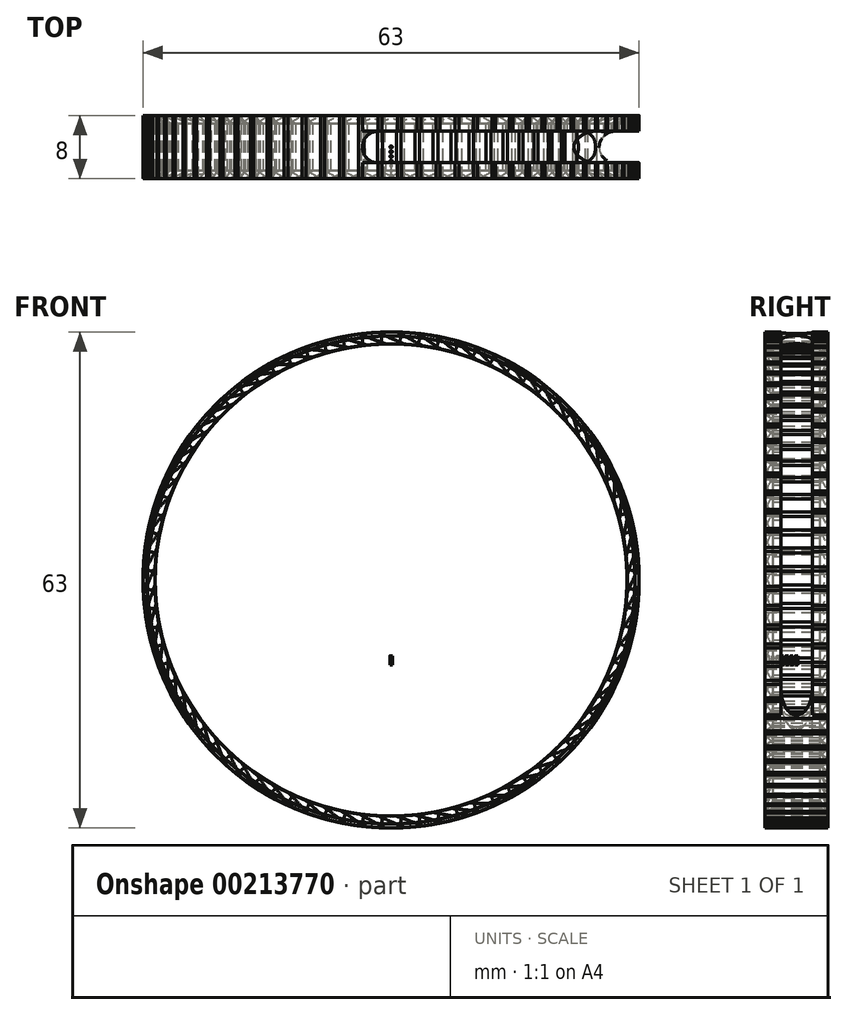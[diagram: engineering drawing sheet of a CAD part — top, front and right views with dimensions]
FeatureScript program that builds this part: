
annotation { "Feature Type Name" : "Feature", "Feature Type Description" : "" }
export const myFeature = defineFeature(function(context is Context, id is Id, definition is map)
    precondition{}
    {
        {
            var Q0;
            Q0=qCreatedBy(makeId("Front.planeOp"),FACE);
            var sketch = newSketch(context, id + "F0", { "sketchPlane" : qUnion([Q0])});
            skCircle(sketch, "E0", {"center": v(0, 0) * mm, "radius": 30 * mm});
            skCircle(sketch, "E1.0", {"center": v(0, 0) * mm, "radius": 31.5 * mm});
            skLineSegment(sketch, "E2.bottom", {"start": v(3.63, 31.29) * mm, "end": v(-3.63, 31.29) * mm, "construction": true});
            skLineSegment(sketch, "E2.top", {"start": v(3.63, 33.45) * mm, "end": v(-3.63, 33.45) * mm});
            skLineSegment(sketch, "E2.left", {"start": v(3.63, 31.29) * mm, "end": v(3.63, 33.45) * mm});
            skLineSegment(sketch, "E2.right", {"start": v(-3.63, 31.29) * mm, "end": v(-3.63, 33.45) * mm});
            skPoint(sketch, "E2.middle", {"position": v(0, 32.37) * mm});
            skLineSegment(sketch, "E3.1.0", {"start": v(6.4, -37.09) * mm, "end": v(4.54, -38.16) * mm});
            skLineSegment(sketch, "E3.1.1", {"start": v(2.77, -30.8) * mm, "end": v(0.9, -31.87) * mm});
            skLineSegment(sketch, "E3.1.2", {"start": v(0.9, -31.87) * mm, "end": v(4.54, -38.16) * mm});
            skLineSegment(sketch, "E3.1.3", {"start": v(2.77, -30.8) * mm, "end": v(6.4, -37.09) * mm, "construction": true});
            skLineSegment(sketch, "E3.2.0", {"start": v(60.6, 5.8) * mm, "end": v(62.47, 4.72) * mm});
            skLineSegment(sketch, "E3.2.1", {"start": v(56.97, -0.5) * mm, "end": v(58.84, -1.58) * mm});
            skLineSegment(sketch, "E3.2.2", {"start": v(58.84, -1.58) * mm, "end": v(62.47, 4.72) * mm});
            skLineSegment(sketch, "E3.2.3", {"start": v(56.97, -0.5) * mm, "end": v(60.6, 5.8) * mm, "construction": true});
            skPoint(sketch, "E3.center", {"position": v(21.12, 0) * mm});
            skLineSegment(sketch, "E4", {"start": v(0, 0) * mm, "end": v(22.27, 22.27) * mm, "construction": true});
            skLineSegment(sketch, "E5", {"start": v(0, 0) * mm, "end": v(-22.27, 22.27) * mm, "construction": true});
            skLineSegment(sketch, "E6.MirrorCS", {"start": v(0, 0) * mm, "end": v(22.27, -22.27) * mm, "construction": true});
            skLineSegment(sketch, "E7.MirrorCS", {"start": v(0, 0) * mm, "end": v(-22.27, -22.27) * mm, "construction": true});
            skLineSegment(sketch, "E8.0", {"start": v(-0.14, 0.14) * mm, "end": v(0, 0.28) * mm});
            skLineSegment(sketch, "E9.MirrorCS", {"start": v(0.14, -0.14) * mm, "end": v(0.28, 0) * mm});
            skLineSegment(sketch, "E10.MirrorCS", {"start": v(0.14, 0.14) * mm, "end": v(0, 0.28) * mm});
            skLineSegment(sketch, "E11.MirrorCS", {"start": v(-0.14, -0.14) * mm, "end": v(-0.28, 0) * mm});
            skLineSegment(sketch, "E12.MirrorCS", {"start": v(0.14, 0.14) * mm, "end": v(0.28, 0) * mm});
            skLineSegment(sketch, "E13.MirrorCS", {"start": v(-0.14, -0.14) * mm, "end": v(0, -0.28) * mm});
            skLineSegment(sketch, "E14.MirrorCS", {"start": v(0.14, -0.14) * mm, "end": v(0, -0.28) * mm});
            skLineSegment(sketch, "E15.MirrorCS", {"start": v(-0.14, 0.14) * mm, "end": v(-0.28, 0) * mm});
            skLineSegment(sketch, "E16.trimOffspring", {"start": v(-7.2, -7.48) * mm, "end": v(-21.07, -21.35) * mm, "construction": true});
            skLineSegment(sketch, "E17.trimOffspring", {"start": v(-7.48, -7.2) * mm, "end": v(-21.35, -21.07) * mm, "construction": true});
            skLineSegment(sketch, "E18.trimOffspring", {"start": v(-7.48, 7.2) * mm, "end": v(-21.35, 21.07) * mm, "construction": true});
            skLineSegment(sketch, "E19.trimOffspring", {"start": v(-7.2, 7.48) * mm, "end": v(-21.07, 21.35) * mm, "construction": true});
            skLineSegment(sketch, "E20.trimOffspring", {"start": v(7.2, 7.48) * mm, "end": v(21.07, 21.35) * mm, "construction": true});
            skLineSegment(sketch, "E21.trimOffspring", {"start": v(7.48, 7.2) * mm, "end": v(21.35, 21.07) * mm, "construction": true});
            skLineSegment(sketch, "E22.trimOffspring", {"start": v(7.2, -7.48) * mm, "end": v(21.07, -21.35) * mm, "construction": true});
            skLineSegment(sketch, "E23.trimOffspring", {"start": v(7.48, -7.2) * mm, "end": v(21.35, -21.07) * mm, "construction": true});
            skLineSegment(sketch, "E24", {"start": v(-3.63, 31.29) * mm, "end": v(-3.63, 28.18) * mm});
            skLineSegment(sketch, "E25", {"start": v(-3.63, 28.18) * mm, "end": v(3.63, 28.18) * mm});
            skLineSegment(sketch, "E26", {"start": v(3.63, 28.18) * mm, "end": v(3.63, 31.29) * mm});
            skLineSegment(sketch, "E27", {"start": v(70.64, 0) * mm, "end": v(60.6, 5.8) * mm});
            skLineSegment(sketch, "E28", {"start": v(56.97, -0.5) * mm, "end": v(28.25, 16.09) * mm});
            skLineSegment(sketch, "E29", {"start": v(28.25, 16.09) * mm, "end": v(70.64, 0) * mm});
            skLineSegment(sketch, "E30", {"start": v(6.4, -37.09) * mm, "end": v(35.16, -20.48) * mm});
            skLineSegment(sketch, "E31", {"start": v(2.77, -30.8) * mm, "end": v(31.56, -14.17) * mm});
            skLineSegment(sketch, "E32", {"start": v(31.56, -14.17) * mm, "end": v(35.16, -20.48) * mm});
            skSolve(sketch);
        }
        {
            var Q0;
            Q0=makeQuery(id+"F0.imprint","IMPRINT",FACE,{"disambiguationData":[TD([[makeQuery(id+"F0.imprint","IMPRINT",EDGE,{"derivedFrom":sQuery(id+"F0.wireOp",EDGE,"E0")}),-1.0]])]});
            var Q1;
            {var subQ2=sQuery(id+"F0.wireOp",EDGE,"E16.trimOffspring");var subQ7=sQuery(id+"F0.wireOp",EDGE,"E0");var subQ9=makeQuery(id+"F0.imprint","INTERSECT",VERTEX,{"derivedFrom":[subQ7,subQ2]});Q1=makeQuery(id+"F0.imprint","IMPRINT",FACE,{"disambiguationData":[TD([[makeQuery(id+"F0.imprint","IMPRINT",EDGE,{"disambiguationData":[TD([[subQ9,-1.0]])],"derivedFrom":subQ7}),-1.0]])]});}
            var Q2;
            {var subQ5=sQuery(id+"F0.wireOp",EDGE,"E21.trimOffspring");var subQ7=sQuery(id+"F0.wireOp",EDGE,"E0");var subQ8=makeQuery(id+"F0.imprint","INTERSECT",VERTEX,{"derivedFrom":[subQ7,subQ5]});Q2=makeQuery(id+"F0.imprint","IMPRINT",FACE,{"disambiguationData":[TD([[makeQuery(id+"F0.imprint","IMPRINT",EDGE,{"disambiguationData":[TD([[subQ8,1.0]])],"derivedFrom":subQ7}),-1.0]])]});}
            var Q3;
            {var subQ2=sQuery(id+"F0.wireOp",EDGE,"E19.trimOffspring");var subQ7=sQuery(id+"F0.wireOp",EDGE,"E0");var subQ8=makeQuery(id+"F0.imprint","INTERSECT",VERTEX,{"derivedFrom":[subQ7,subQ2]});Q3=makeQuery(id+"F0.imprint","IMPRINT",FACE,{"disambiguationData":[TD([[makeQuery(id+"F0.imprint","IMPRINT",EDGE,{"disambiguationData":[TD([[subQ8,1.0]])],"derivedFrom":subQ7}),-1.0]])]});}
            var Q4;
            {var subQ5=sQuery(id+"F0.wireOp",EDGE,"E17.trimOffspring");var subQ6=sQuery(id+"F0.wireOp",EDGE,"E0");var subQ7=makeQuery(id+"F0.imprint","INTERSECT",VERTEX,{"derivedFrom":[subQ6,subQ5]});Q4=makeQuery(id+"F0.imprint","IMPRINT",FACE,{"disambiguationData":[TD([[makeQuery(id+"F0.imprint","IMPRINT",EDGE,{"disambiguationData":[TD([[subQ7,1.0]])],"derivedFrom":subQ6}),-1.0]])]});}
            extrude(context, id + "F1", {"entities" : qUnion([Q0, Q1, Q2, Q3, Q4]), "depth" : 4 * mm, "hasSecondDirection" : true, "secondDirectionOppositeDirection" : true, "secondDirectionDepth" : 4 * mm});
        }
        {
            var Q0;
            Q0=makeQuery(id+"F1.opExtrude","CAP_EDGE",EDGE,{"disambiguationData":[OSD([sQuery(id+"F0.wireOp",EDGE,"E0")])],"isStart":false});
            var Q1;
            Q1=makeQuery(id+"F1.opExtrude","CAP_EDGE",EDGE,{"disambiguationData":[OSD([sQuery(id+"F0.wireOp",EDGE,"E0")])],"isStart":true});
            chamfer(context, id + "F2", {"entities" : qUnion([Q0, Q1]), "width" : 1 * mm, "tangentPropagation" : true});
        }
        {
            var Q0;
            Q0=qCreatedBy(makeId("Top.planeOp"),FACE);
            var sketch = newSketch(context, id + "F3", { "sketchPlane" : qUnion([Q0])});
            skCircle(sketch, "E33", {"center": v(0, 0) * mm, "radius": 0.15 * mm});
            skCircle(sketch, "E34.1.0.0", {"center": v(0, -0.6) * mm, "radius": 0.15 * mm});
            skCircle(sketch, "E34.2.0.0", {"center": v(0, -1.2) * mm, "radius": 0.15 * mm});
            skCircle(sketch, "E34.3.0.0", {"center": v(0, -1.8) * mm, "radius": 0.15 * mm});
            skCircle(sketch, "E34.4.0.0", {"center": v(0, -2.4) * mm, "radius": 0.15 * mm});
            skCircle(sketch, "E34.5.0.0", {"center": v(0, -3) * mm, "radius": 0.15 * mm});
            skCircle(sketch, "E34.6.0.0", {"center": v(0, -3.6) * mm, "radius": 0.15 * mm});
            skLineSegment(sketch, "E34.direction1", {"start": v(0, 0) * mm, "end": v(0, -0.6) * mm, "construction": true});
            skCircle(sketch, "E35.MirrorC", {"center": v(0, 0.6) * mm, "radius": 0.15 * mm});
            skCircle(sketch, "E36.MirrorC", {"center": v(0, 1.2) * mm, "radius": 0.15 * mm});
            skCircle(sketch, "E37.MirrorC", {"center": v(0, 1.8) * mm, "radius": 0.15 * mm});
            skCircle(sketch, "E38.MirrorC", {"center": v(0, 2.4) * mm, "radius": 0.15 * mm});
            skCircle(sketch, "E39.MirrorC", {"center": v(0, 3) * mm, "radius": 0.15 * mm});
            skCircle(sketch, "E40.MirrorC", {"center": v(0, 3.6) * mm, "radius": 0.15 * mm});
            skSolve(sketch);
        }
        {
            var Q0;
            Q0=makeQuery(id+"F3.imprint","IMPRINT",FACE,{"disambiguationData":[TD([[makeQuery(id+"F3.imprint","IMPRINT",EDGE,{"derivedFrom":sQuery(id+"F3.wireOp",EDGE,"E33")}),1.0]])]});
            var Q1;
            Q1=makeQuery(id+"F3.imprint","IMPRINT",FACE,{"disambiguationData":[TD([[makeQuery(id+"F3.imprint","IMPRINT",EDGE,{"derivedFrom":sQuery(id+"F3.wireOp",EDGE,"E35.MirrorC")}),-1.0]])]});
            var Q2;
            Q2=makeQuery(id+"F3.imprint","IMPRINT",FACE,{"disambiguationData":[TD([[makeQuery(id+"F3.imprint","IMPRINT",EDGE,{"derivedFrom":sQuery(id+"F3.wireOp",EDGE,"E36.MirrorC")}),-1.0]])]});
            var Q3;
            Q3=makeQuery(id+"F3.imprint","IMPRINT",FACE,{"disambiguationData":[TD([[makeQuery(id+"F3.imprint","IMPRINT",EDGE,{"derivedFrom":sQuery(id+"F3.wireOp",EDGE,"E37.MirrorC")}),-1.0]])]});
            var Q4;
            Q4=makeQuery(id+"F3.imprint","IMPRINT",FACE,{"disambiguationData":[TD([[makeQuery(id+"F3.imprint","IMPRINT",EDGE,{"derivedFrom":sQuery(id+"F3.wireOp",EDGE,"E38.MirrorC")}),-1.0]])]});
            var Q5;
            Q5=makeQuery(id+"F3.imprint","IMPRINT",FACE,{"disambiguationData":[TD([[makeQuery(id+"F3.imprint","IMPRINT",EDGE,{"derivedFrom":sQuery(id+"F3.wireOp",EDGE,"E39.MirrorC")}),-1.0]])]});
            var Q6;
            Q6=makeQuery(id+"F3.imprint","IMPRINT",FACE,{"disambiguationData":[TD([[makeQuery(id+"F3.imprint","IMPRINT",EDGE,{"derivedFrom":sQuery(id+"F3.wireOp",EDGE,"E40.MirrorC")}),-1.0]])]});
            var Q7;
            Q7=makeQuery(id+"F3.imprint","IMPRINT",FACE,{"disambiguationData":[TD([[makeQuery(id+"F3.imprint","IMPRINT",EDGE,{"derivedFrom":sQuery(id+"F3.wireOp",EDGE,"E34.1.0.0")}),1.0]])]});
            var Q8;
            Q8=makeQuery(id+"F3.imprint","IMPRINT",FACE,{"disambiguationData":[TD([[makeQuery(id+"F3.imprint","IMPRINT",EDGE,{"derivedFrom":sQuery(id+"F3.wireOp",EDGE,"E34.2.0.0")}),1.0]])]});
            var Q9;
            Q9=makeQuery(id+"F3.imprint","IMPRINT",FACE,{"disambiguationData":[TD([[makeQuery(id+"F3.imprint","IMPRINT",EDGE,{"derivedFrom":sQuery(id+"F3.wireOp",EDGE,"E34.3.0.0")}),1.0]])]});
            var Q10;
            Q10=makeQuery(id+"F3.imprint","IMPRINT",FACE,{"disambiguationData":[TD([[makeQuery(id+"F3.imprint","IMPRINT",EDGE,{"derivedFrom":sQuery(id+"F3.wireOp",EDGE,"E34.4.0.0")}),1.0]])]});
            var Q11;
            Q11=makeQuery(id+"F3.imprint","IMPRINT",FACE,{"disambiguationData":[TD([[makeQuery(id+"F3.imprint","IMPRINT",EDGE,{"derivedFrom":sQuery(id+"F3.wireOp",EDGE,"E34.5.0.0")}),1.0]])]});
            var Q12;
            Q12=makeQuery(id+"F3.imprint","IMPRINT",FACE,{"disambiguationData":[TD([[makeQuery(id+"F3.imprint","IMPRINT",EDGE,{"derivedFrom":sQuery(id+"F3.wireOp",EDGE,"E34.6.0.0")}),1.0]])]});
            extrude(context, id + "F4", {"entities" : qUnion([Q0, Q1, Q2, Q3, Q4, Q5, Q6, Q7, Q8, Q9, Q10, Q11, Q12]), "operationType" : NewBodyOperationType.ADD, "oppositeDirection" : true, "depth" : ((17.75 / 2) + 1.9) * mm, "hasSecondDirection" : true, "secondDirectionOppositeDirection" : true, "secondDirectionDepth" : 9.62 * mm});
        }
        {
            var Q0;
            Q0=makeQuery(id+"F1.opExtrude","SWEPT_BODY",BODY,{"disambiguationData":[OSD([sQuery(id+"F0.wireOp",EDGE,"E0"),sQuery(id+"F0.wireOp",EDGE,"E1.0")])]});
            var Q1;
            Q1=makeQuery(id+"F1.opExtrude","CAP_EDGE",EDGE,{"disambiguationData":[OSD([sQuery(id+"F0.wireOp",EDGE,"E1.0")])],"isStart":false});
            circularPattern(context, id + "F5", {"operationType" : NewBodyOperationType.ADD, "entities" : qUnion([Q0]), "axis" : qUnion([Q1]), "angle" : 360 * degree, "instanceCount" : 80, "equalSpace" : true});
        }
        {
            var Q0;
            Q0=makeQuery(id+"F0.imprint","IMPRINT",FACE,{"disambiguationData":[TD([[makeQuery(id+"F0.imprint","IMPRINT",EDGE,{"derivedFrom":sQuery(id+"F0.wireOp",EDGE,"E2.top")}),1.0]])]});
            var Q1;
            {var subQ0=sQuery(id+"F0.wireOp",EDGE,"E24");var subQ1=sQuery(id+"F0.wireOp",EDGE,"E0");var subQ2=makeQuery(id+"F0.imprint","INTERSECT",VERTEX,{"derivedFrom":[subQ1,subQ0]});Q1=makeQuery(id+"F0.imprint","IMPRINT",FACE,{"disambiguationData":[TD([[makeQuery(id+"F0.imprint","IMPRINT",EDGE,{"disambiguationData":[TD([[subQ2,1.0]])],"derivedFrom":subQ1}),-1.0]])]});}
            var Q2;
            {var subQ5=sQuery(id+"F0.wireOp",EDGE,"E25");Q2=makeQuery(id+"F0.imprint","IMPRINT",FACE,{"disambiguationData":[TD([[makeQuery(id+"F0.imprint","IMPRINT",EDGE,{"derivedFrom":subQ5}),1.0]])]});}
            var Q3;
            {var subQ5=sQuery(id+"F0.wireOp",EDGE,"E29");Q3=makeQuery(id+"F0.imprint","IMPRINT",FACE,{"disambiguationData":[TD([[makeQuery(id+"F0.imprint","IMPRINT",EDGE,{"derivedFrom":subQ5}),-1.0]])]});}
            var Q4;
            {var subQ0=sQuery(id+"F0.wireOp",EDGE,"E28");var subQ1=sQuery(id+"F0.wireOp",EDGE,"E0");var subQ2=makeQuery(id+"F0.imprint","INTERSECT",VERTEX,{"derivedFrom":[subQ1,subQ0]});Q4=makeQuery(id+"F0.imprint","IMPRINT",FACE,{"disambiguationData":[TD([[makeQuery(id+"F0.imprint","IMPRINT",EDGE,{"disambiguationData":[TD([[subQ2,-1.0]])],"derivedFrom":subQ1}),-1.0]])]});}
            var Q5;
            {var subQ0=sQuery(id+"F0.wireOp",EDGE,"E3.2.0");Q5=makeQuery(id+"F0.imprint","IMPRINT",FACE,{"disambiguationData":[TD([[makeQuery(id+"F0.imprint","IMPRINT",EDGE,{"derivedFrom":subQ0}),-1.0]])]});}
            var Q6;
            {var subQ5=sQuery(id+"F0.wireOp",EDGE,"E32");Q6=makeQuery(id+"F0.imprint","IMPRINT",FACE,{"disambiguationData":[TD([[makeQuery(id+"F0.imprint","IMPRINT",EDGE,{"derivedFrom":subQ5}),-1.0]])]});}
            var Q7;
            {var subQ0=sQuery(id+"F0.wireOp",EDGE,"E3.1.0");Q7=makeQuery(id+"F0.imprint","IMPRINT",FACE,{"disambiguationData":[TD([[makeQuery(id+"F0.imprint","IMPRINT",EDGE,{"derivedFrom":subQ0}),-1.0]])]});}
            var Q8;
            {var subQ0=sQuery(id+"F0.wireOp",EDGE,"E31");var subQ1=sQuery(id+"F0.wireOp",EDGE,"E0");var subQ2=makeQuery(id+"F0.imprint","INTERSECT",VERTEX,{"derivedFrom":[subQ1,subQ0]});Q8=makeQuery(id+"F0.imprint","IMPRINT",FACE,{"disambiguationData":[TD([[makeQuery(id+"F0.imprint","IMPRINT",EDGE,{"disambiguationData":[TD([[subQ2,-1.0]])],"derivedFrom":subQ1}),-1.0]])]});}
            extrude(context, id + "F6", {"entities" : qUnion([Q0, Q1, Q2, Q3, Q4, Q5, Q6, Q7, Q8]), "operationType" : NewBodyOperationType.REMOVE, "oppositeDirection" : true, "depth" : 2 * mm, "hasSecondDirection" : true, "secondDirectionOppositeDirection" : false, "secondDirectionDepth" : 2 * mm});
        }
        {
            var Q0;
            Q0=makeQuery(id+"F6.boolean.opBoolean","COPY",EDGE,{"derivedFrom":makeQuery(id+"F6.opExtrude","CAP_EDGE",EDGE,{"disambiguationData":[OSD([sQuery(id+"F0.wireOp",EDGE,"E3.2.1"),sQuery(id+"F0.wireOp",EDGE,"E28")])],"isStart":false})});
            var Q1;
            Q1=makeQuery(id+"F6.boolean.opBoolean","COPY",EDGE,{"derivedFrom":makeQuery(id+"F6.opExtrude","CAP_EDGE",EDGE,{"disambiguationData":[OSD([sQuery(id+"F0.wireOp",EDGE,"E3.2.0"),sQuery(id+"F0.wireOp",EDGE,"E27")])],"isStart":false})});
            var Q2;
            Q2=makeQuery(id+"F6.boolean.opBoolean","COPY",EDGE,{"derivedFrom":makeQuery(id+"F6.opExtrude","CAP_EDGE",EDGE,{"disambiguationData":[OSD([sQuery(id+"F0.wireOp",EDGE,"E3.2.0"),sQuery(id+"F0.wireOp",EDGE,"E27")])],"isStart":true})});
            var Q3;
            Q3=makeQuery(id+"F6.boolean.opBoolean","COPY",EDGE,{"derivedFrom":makeQuery(id+"F6.opExtrude","CAP_EDGE",EDGE,{"disambiguationData":[OSD([sQuery(id+"F0.wireOp",EDGE,"E3.2.1"),sQuery(id+"F0.wireOp",EDGE,"E28")])],"isStart":true})});
            var Q4;
            Q4=makeQuery(id+"F6.boolean.opBoolean","COPY",EDGE,{"derivedFrom":makeQuery(id+"F6.opExtrude","CAP_EDGE",EDGE,{"disambiguationData":[OSD([sQuery(id+"F0.wireOp",EDGE,"E3.1.0"),sQuery(id+"F0.wireOp",EDGE,"E30")])],"isStart":false})});
            var Q5;
            Q5=makeQuery(id+"F6.boolean.opBoolean","COPY",EDGE,{"derivedFrom":makeQuery(id+"F6.opExtrude","CAP_EDGE",EDGE,{"disambiguationData":[OSD([sQuery(id+"F0.wireOp",EDGE,"E3.1.1"),sQuery(id+"F0.wireOp",EDGE,"E31")])],"isStart":false})});
            var Q6;
            Q6=makeQuery(id+"F6.boolean.opBoolean","COPY",EDGE,{"derivedFrom":makeQuery(id+"F6.opExtrude","CAP_EDGE",EDGE,{"disambiguationData":[OSD([sQuery(id+"F0.wireOp",EDGE,"E3.1.1"),sQuery(id+"F0.wireOp",EDGE,"E31")])],"isStart":true})});
            var Q7;
            Q7=makeQuery(id+"F6.boolean.opBoolean","COPY",EDGE,{"derivedFrom":makeQuery(id+"F6.opExtrude","CAP_EDGE",EDGE,{"disambiguationData":[OSD([sQuery(id+"F0.wireOp",EDGE,"E3.1.0"),sQuery(id+"F0.wireOp",EDGE,"E30")])],"isStart":true})});
            var Q8;
            Q8=makeQuery(id+"F6.boolean.opBoolean","COPY",EDGE,{"derivedFrom":makeQuery(id+"F6.opExtrude","CAP_EDGE",EDGE,{"disambiguationData":[OSD([sQuery(id+"F0.wireOp",EDGE,"E2.right"),sQuery(id+"F0.wireOp",EDGE,"E24")])],"isStart":false})});
            var Q9;
            Q9=makeQuery(id+"F6.boolean.opBoolean","COPY",EDGE,{"derivedFrom":makeQuery(id+"F6.opExtrude","CAP_EDGE",EDGE,{"disambiguationData":[OSD([sQuery(id+"F0.wireOp",EDGE,"E2.left"),sQuery(id+"F0.wireOp",EDGE,"E26")])],"isStart":false})});
            var Q10;
            Q10=makeQuery(id+"F6.boolean.opBoolean","COPY",EDGE,{"derivedFrom":makeQuery(id+"F6.opExtrude","CAP_EDGE",EDGE,{"disambiguationData":[OSD([sQuery(id+"F0.wireOp",EDGE,"E2.right"),sQuery(id+"F0.wireOp",EDGE,"E24")])],"isStart":true})});
            var Q11;
            Q11=makeQuery(id+"F6.boolean.opBoolean","COPY",EDGE,{"derivedFrom":makeQuery(id+"F6.opExtrude","CAP_EDGE",EDGE,{"disambiguationData":[OSD([sQuery(id+"F0.wireOp",EDGE,"E2.left"),sQuery(id+"F0.wireOp",EDGE,"E26")])],"isStart":true})});
            fillet(context, id + "F7", {"entities" : qUnion([Q0, Q1, Q2, Q3, Q4, Q5, Q6, Q7, Q8, Q9, Q10, Q11]), "radius" : 1.94 * mm, "tangentPropagation" : true, "allowEdgeOverflow" : false});
        }
    });
